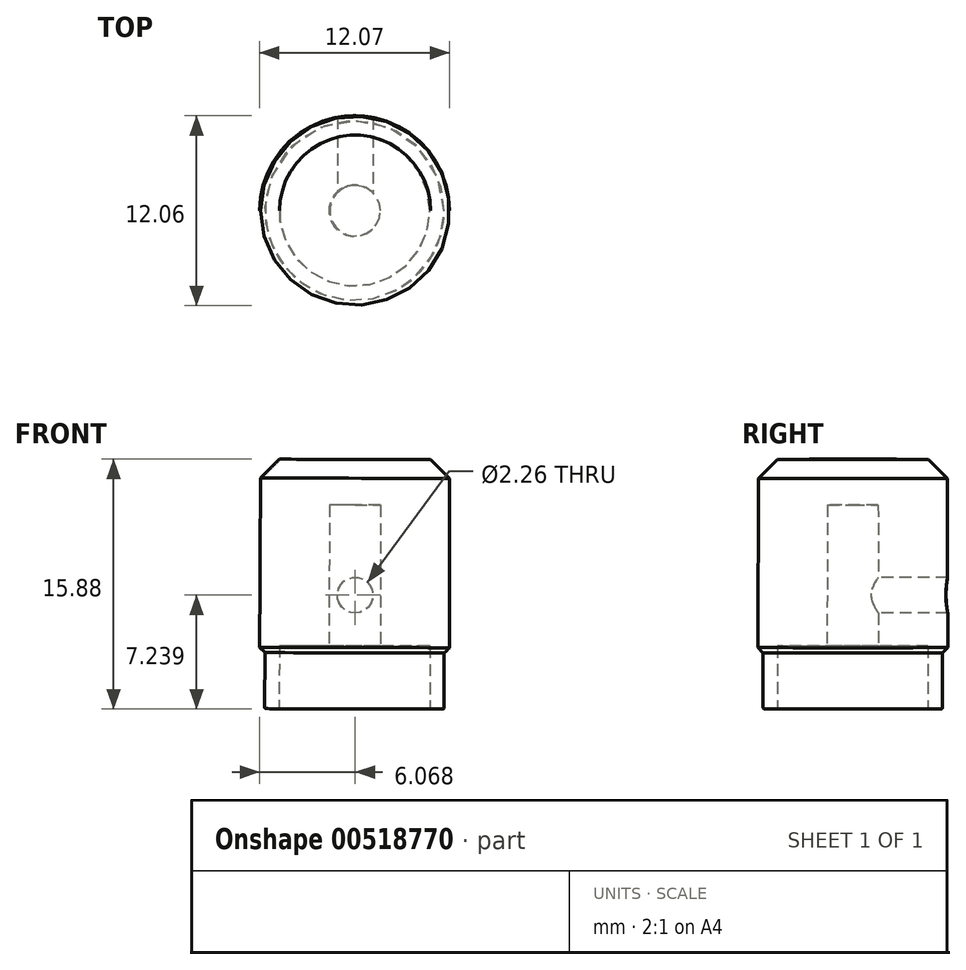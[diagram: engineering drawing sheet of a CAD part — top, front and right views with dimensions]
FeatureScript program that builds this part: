
annotation { "Feature Type Name" : "Feature", "Feature Type Description" : "" }
export const myFeature = defineFeature(function(context is Context, id is Id, definition is map)
    precondition{}
    {
        {
            var Q0;
            Q0=qCreatedBy(makeId("Front.planeOp"),FACE);
            var sketch = newSketch(context, id + "F0", { "sketchPlane" : qUnion([Q0])});
            skLineSegment(sketch, "E0.bottom", {"start": v(4.75, 0) * mm, "end": v(5.67, 0) * mm});
            skLineSegment(sketch, "E0.top", {"start": v(0, 15.85) * mm, "end": v(6, 15.85) * mm});
            skLineSegment(sketch, "E0.left", {"start": v(0, 4) * mm, "end": v(0, 15.85) * mm, "construction": true});
            skLineSegment(sketch, "E0.right", {"start": v(6, 2.7) * mm, "end": v(6, 15.85) * mm});
            skLineSegment(sketch, "E1", {"start": v(1.6, 4) * mm, "end": v(4.75, 4) * mm});
            skLineSegment(sketch, "E2", {"start": v(4.75, 4) * mm, "end": v(4.75, 0) * mm});
            skLineSegment(sketch, "E3", {"start": v(5.67, 0) * mm, "end": v(5.67, 2.7) * mm});
            skLineSegment(sketch, "E4", {"start": v(5.67, 2.7) * mm, "end": v(6, 2.7) * mm});
            skLineSegment(sketch, "E5", {"start": v(1.6, 4) * mm, "end": v(1.6, 12.95) * mm});
            skLineSegment(sketch, "E6", {"start": v(1.6, 12.95) * mm, "end": v(0, 12.95) * mm});
            skLineSegment(sketch, "E7", {"start": v(0, 15.85) * mm, "end": v(0, 12.95) * mm});
            skPoint(sketch, "E8", {"position": v(0, 7.24) * mm});
            skSolve(sketch);
        }
        {
            var Q0;
            Q0 = qSketchRegion(id + "F0", true);
            var Q1;
            Q1=sQuery(id+"F0.wireOp",EDGE,"E7");
            revolve(context, id + "F1", {"entities" : qUnion([Q0]), "axis" : qUnion([Q1]), "revolveType" : RevolveType.FULL});
        }
        {
            var Q0;
            Q0=makeQuery(id+"F1.opRevolve","SWEPT_EDGE",EDGE,{"disambiguationData":[OSD([sQuery(id+"F0.wireOp",EDGE,"E0.right"),sQuery(id+"F0.wireOp",EDGE,"1gA7HIHt-x4nL-bbab-XW26-70b5hIUI0d57")])]});
            var Q1;
            Q1=makeQuery(id+"F1.opRevolve","SWEPT_EDGE",EDGE,{"disambiguationData":[OSD([sQuery(id+"F0.wireOp",EDGE,"E0.right"),sQuery(id+"F0.wireOp",EDGE,"E4")])]});
            var Q2;
            Q2=makeQuery(id+"F1.opRevolve","SWEPT_EDGE",EDGE,{"disambiguationData":[OSD([sQuery(id+"F0.wireOp",EDGE,"E0.top"),sQuery(id+"F0.wireOp",EDGE,"q5wVps5m-LlMx-Xk9N-7oXw-UMo5WSRKdbD1")])]});
            chamfer(context, id + "F2", {"entities" : qUnion([Q0, Q1, Q2]), "width" : 1.2 * mm, "tangentPropagation" : true});
        }
        {
            var Q0;
            Q0=makeQuery(id+"F1.opRevolve","SWEPT_EDGE",EDGE,{"disambiguationData":[OSD([sQuery(id+"F0.wireOp",EDGE,"E0.bottom"),sQuery(id+"F0.wireOp",EDGE,"E3")])]});
            fillet(context, id + "F3", {"entities" : qUnion([Q0]), "radius" : .1 * mm, "tangentPropagation" : true, "allowEdgeOverflow" : false});
        }
        {
            var Q0;
            Q0=sQuery(id+"F0.wireOp",VERTEX,"E8");
            var Q1;
            Q1=makeQuery(id+"F1.opRevolve","SWEPT_BODY",BODY,{"disambiguationData":[OSD([sQuery(id+"F0.wireOp",EDGE,"E0.bottom"),sQuery(id+"F0.wireOp",EDGE,"E0.top"),sQuery(id+"F0.wireOp",EDGE,"E0.right"),sQuery(id+"F0.wireOp",EDGE,"E1"),sQuery(id+"F0.wireOp",EDGE,"E2"),sQuery(id+"F0.wireOp",EDGE,"E3"),sQuery(id+"F0.wireOp",EDGE,"E4"),sQuery(id+"F0.wireOp",EDGE,"q5wVps5m-LlMx-Xk9N-7oXw-UMo5WSRKdbD1"),sQuery(id+"F0.wireOp",EDGE,"1gA7HIHt-x4nL-bbab-XW26-70b5hIUI0d57"),sQuery(id+"F0.wireOp",EDGE,"E5"),sQuery(id+"F0.wireOp",EDGE,"E6"),sQuery(id+"F0.wireOp",EDGE,"E7")])]});
            hole(context, id + "F4", {"style" : HoleStyle.SIMPLE, "endStyle" : HoleEndStyle.THROUGH, "standardTappedOrClearance" : lookupTablePath({ "standard" : "ANSI", "engagement" : "75%", "pitch" : "40 tpi", "size" : "#4", "type" : "Tapped" }), "standardBlindInLast" : lookupTablePath({ "standard" : "ANSI", "engagement" : "75%", "pitch" : "40 tpi", "size" : "#4", "type" : "Tapped" }), "holeDiameter" : 2.26 * mm, "showTappedDepth" : true, "isTappedThrough" : true, "tappedDepth" : 12 * mm, "tapClearance" : 3, "locations" : qUnion([Q0]), "scope" : qUnion([Q1]), "majorDiameter" : 2.84 * mm});
        }
    });
